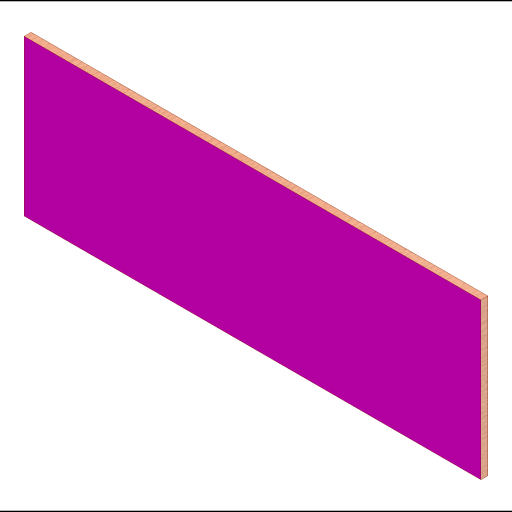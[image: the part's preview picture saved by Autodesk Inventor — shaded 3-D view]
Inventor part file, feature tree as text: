
AUTODESK INVENTOR PART (.ipt)
format: ipt  version: 2023 (Build 270158000, 158)  size: 99,328 bytes
history: native  units: in
note: dims shown in document units (in); Inventor stores cm internally (conversion verified against a paired STEP export)
features: extrude x1, sketch x1
ambient origin geometry x8: Origin, YZ Plane, XZ Plane, XY Plane, X Axis, Y Axis, Z Axis, Center Point
bodies: Solid1 (feature_tree)
feature tree (2):
  extrude  "Extrusion1"  Depth=11.25in
  sketch  "Sketch1"  dims[d0=33.0in d1=11.25in d2=0.5in d3=0.0in]
